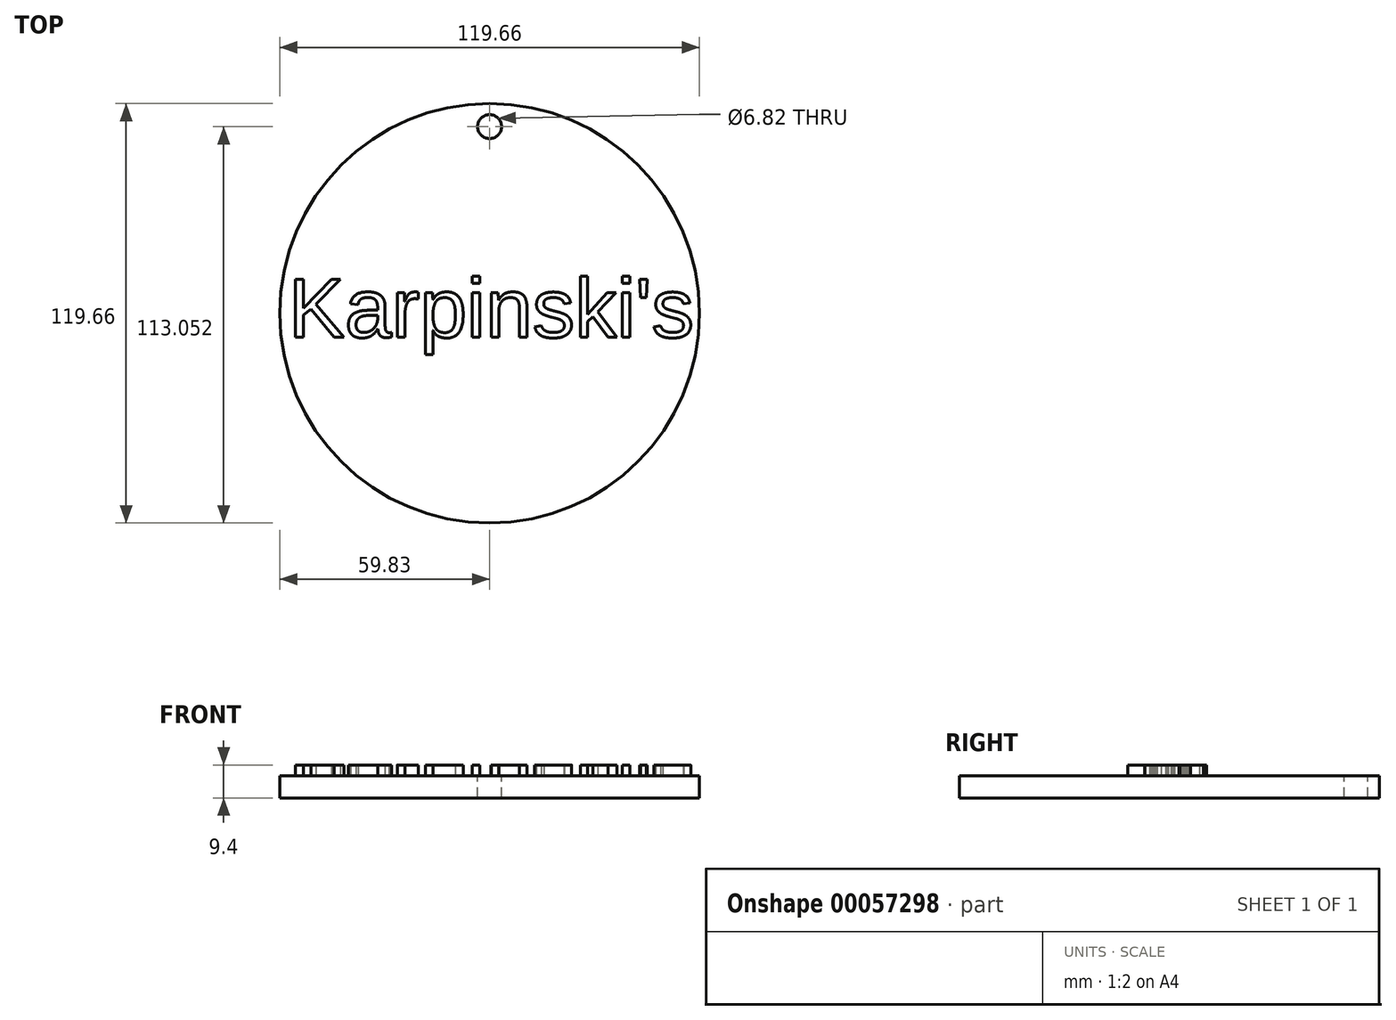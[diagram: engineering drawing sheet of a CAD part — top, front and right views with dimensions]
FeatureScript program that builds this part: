
annotation { "Feature Type Name" : "Feature", "Feature Type Description" : "" }
export const myFeature = defineFeature(function(context is Context, id is Id, definition is map)
    precondition{}
    {
        {
            var Q0;
            Q0=qCreatedBy(makeId("Top.planeOp"),FACE);
            var sketch = newSketch(context, id + "F0", { "sketchPlane" : qUnion([Q0])});
            skCircle(sketch, "E0", {"center": v(0, 0) * mm, "radius": 59.83 * mm});
            skSolve(sketch);
        }
        {
            var Q0;
            Q0 = qSketchRegion(id + "F0", true);
            extrude(context, id + "F1", {"entities" : qUnion([Q0]), "depth" : 6.35 * mm});
        }
        {
            var Q0;
            Q0=makeQuery(id+"F1.opExtrude","CAP_FACE",FACE,{"disambiguationData":[OSD([sQuery(id+"F0.wireOp",EDGE,"E0")])],"isStart":false});
            var sketch = newSketch(context, id + "F2", { "sketchPlane" : qUnion([Q0])});
            skText(sketch, "E1", { "text": "Karpinski\'s", "fontName": "Arimo-Regular.ttf"});
            const initialGuessF2  = {"E1": [-0.05733, -0.00684, 1, 0, 0.01732]};
            skSetInitialGuess(sketch, initialGuessF2);
            skSolve(sketch);
        }
        {
            var Q0;
            Q0 = qSketchRegion(id + "F2", true);
            extrude(context, id + "F3", {"entities" : qUnion([Q0]), "operationType" : NewBodyOperationType.ADD, "depth" : 3.05 * mm});
        }
        {
            var Q0;
            {var subQ0=sQuery(id+"F0.wireOp",EDGE,"E0");Q0=makeQuery(id+"F3.boolean.opBoolean","SPLIT",FACE,{"disambiguationData":[TD([makeQuery(id+"F1.opExtrude","SWEPT_FACE",FACE,{"disambiguationData":[OSD([subQ0])]})])],"derivedFrom":makeQuery(id+"F1.opExtrude","CAP_FACE",FACE,{"disambiguationData":[OSD([subQ0])],"isStart":false})});}
            var sketch = newSketch(context, id + "F4", { "sketchPlane" : qUnion([Q0])});
            skCircle(sketch, "E2", {"center": v(0, 53.22) * mm, "radius": 3.41 * mm});
            skSolve(sketch);
        }
        {
            var Q0;
            Q0 = qSketchRegion(id + "F4", true);
            extrude(context, id + "F5", {"entities" : qUnion([Q0]), "operationType" : NewBodyOperationType.REMOVE, "oppositeDirection" : true, "depth" : 25.4 * mm});
        }
    });
